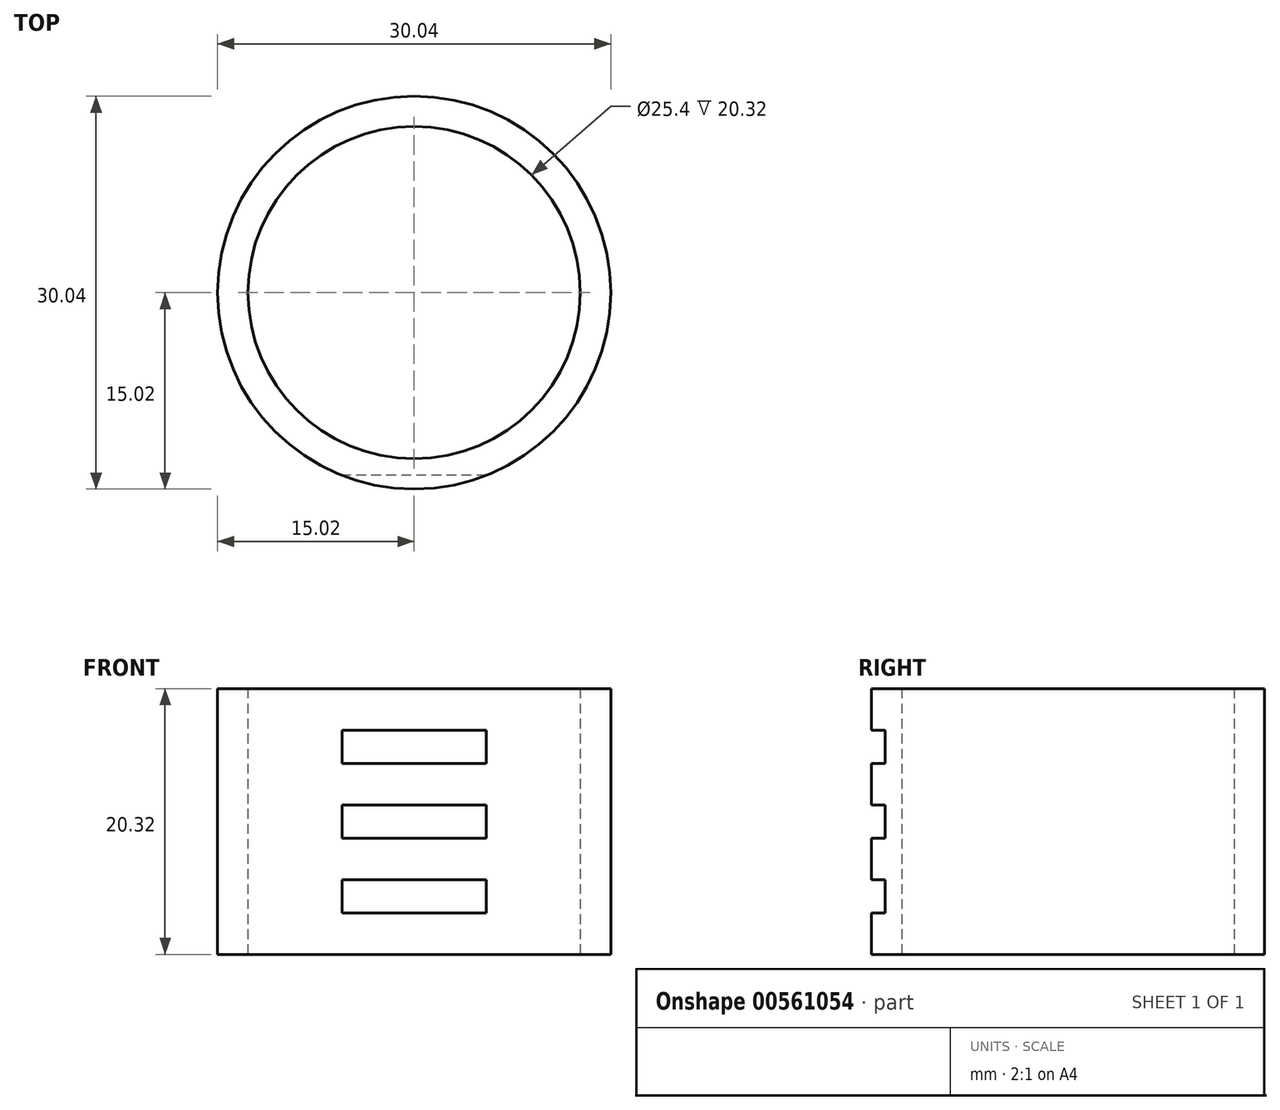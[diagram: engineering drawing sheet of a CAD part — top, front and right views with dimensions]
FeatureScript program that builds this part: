
annotation { "Feature Type Name" : "Feature", "Feature Type Description" : "" }
export const myFeature = defineFeature(function(context is Context, id is Id, definition is map)
    precondition{}
    {
        {
            var Q0;
            Q0=qCreatedBy(makeId("Top.planeOp"),FACE);
            var sketch = newSketch(context, id + "F0", { "sketchPlane" : qUnion([Q0])});
            skCircle(sketch, "E0", {"center": v(0, 0) * mm, "radius": 12.7 * mm});
            skCircle(sketch, "E1", {"center": v(0, 0) * mm, "radius": 15.02 * mm});
            skSolve(sketch);
        }
        {
            var Q0;
            Q0=makeQuery(id+"F0.imprint","IMPRINT",FACE,{"disambiguationData":[TD([[makeQuery(id+"F0.imprint","IMPRINT",EDGE,{"derivedFrom":sQuery(id+"F0.wireOp",EDGE,"E0")}),-1.0]])]});
            extrude(context, id + "F1", {"entities" : qUnion([Q0]), "depth" : 20.32 * mm, "offsetDistance" : 25.4 * mm});
        }
        {
            var Q0;
            Q0=makeQuery(id+"F1.opExtrude","SWEPT_FACE",FACE,{"disambiguationData":[OSD([sQuery(id+"F0.wireOp",EDGE,"E1")])]});
            cPlane(context, id + "F2", {"entities" : qUnion([Q0]), "cplaneType" : CPlaneType.LINE_ANGLE, "offset" : 25.4 * mm, "angle" : 0 * degree, "width" : 152.4 * mm, "height" : 152.4 * mm});
        }
        {
            var Q0;
            Q0=qCreatedBy(id+"F2.planeOp",FACE);
            var sketch = newSketch(context, id + "F3", { "sketchPlane" : qUnion([Q0])});
            skLineSegment(sketch, "E2.bottom", {"start": v(21.59, 11.43) * mm, "end": v(13.97, 11.43) * mm});
            skLineSegment(sketch, "E2.top", {"start": v(21.59, 8.9) * mm, "end": v(13.97, 8.9) * mm});
            skLineSegment(sketch, "E2.left", {"start": v(21.59, 11.43) * mm, "end": v(21.59, 8.9) * mm});
            skLineSegment(sketch, "E2.right", {"start": v(13.97, 11.43) * mm, "end": v(13.97, 8.9) * mm});
            skLineSegment(sketch, "E3.bottom", {"start": v(21.6, 17.14) * mm, "end": v(13.97, 17.14) * mm});
            skLineSegment(sketch, "E3.top", {"start": v(21.6, 14.6) * mm, "end": v(13.97, 14.6) * mm});
            skLineSegment(sketch, "E3.left", {"start": v(21.6, 17.14) * mm, "end": v(21.6, 14.6) * mm});
            skLineSegment(sketch, "E3.right", {"start": v(13.97, 17.14) * mm, "end": v(13.97, 14.6) * mm});
            skLineSegment(sketch, "E4.bottom", {"start": v(21.59, 5.72) * mm, "end": v(13.97, 5.72) * mm});
            skLineSegment(sketch, "E4.top", {"start": v(21.59, 3.18) * mm, "end": v(13.97, 3.17) * mm});
            skLineSegment(sketch, "E4.left", {"start": v(21.59, 5.71) * mm, "end": v(21.59, 3.18) * mm});
            skLineSegment(sketch, "E4.right", {"start": v(13.97, 5.71) * mm, "end": v(13.97, 3.17) * mm});
            skSolve(sketch);
        }
        {
            var Q0;
            Q0=makeQuery(id+"F3.imprint","IMPRINT",FACE,{"disambiguationData":[TD([[makeQuery(id+"F3.imprint","IMPRINT",EDGE,{"derivedFrom":sQuery(id+"F3.wireOp",EDGE,"E2.bottom")}),1.0]])]});
            var Q1;
            Q1=makeQuery(id+"F3.imprint","IMPRINT",FACE,{"disambiguationData":[TD([[makeQuery(id+"F3.imprint","IMPRINT",EDGE,{"derivedFrom":sQuery(id+"F3.wireOp",EDGE,"E3.bottom")}),1.0]])]});
            var Q2;
            Q2=makeQuery(id+"F3.imprint","IMPRINT",FACE,{"disambiguationData":[TD([[makeQuery(id+"F3.imprint","IMPRINT",EDGE,{"derivedFrom":sQuery(id+"F3.wireOp",EDGE,"E4.bottom")}),1.0]])]});
            extrude(context, id + "F4", {"entities" : qUnion([Q0, Q1, Q2]), "operationType" : NewBodyOperationType.REMOVE, "oppositeDirection" : true, "depth" : 25.4 * mm, "offsetDistance" : 25.4 * mm, "hasSecondDirection" : true, "secondDirectionOppositeDirection" : false, "secondDirectionDepth" : 25.4 * mm});
        }
        {
            var Q0;
            Q0=qCreatedBy(makeId("Front.planeOp"),FACE);
            var sketch = newSketch(context, id + "F5", { "sketchPlane" : qUnion([Q0])});
            skLineSegment(sketch, "E5", {"start": v(0, 32.37) * mm, "end": v(0, -36.06) * mm, "construction": true});
            skSolve(sketch);
        }
    });
